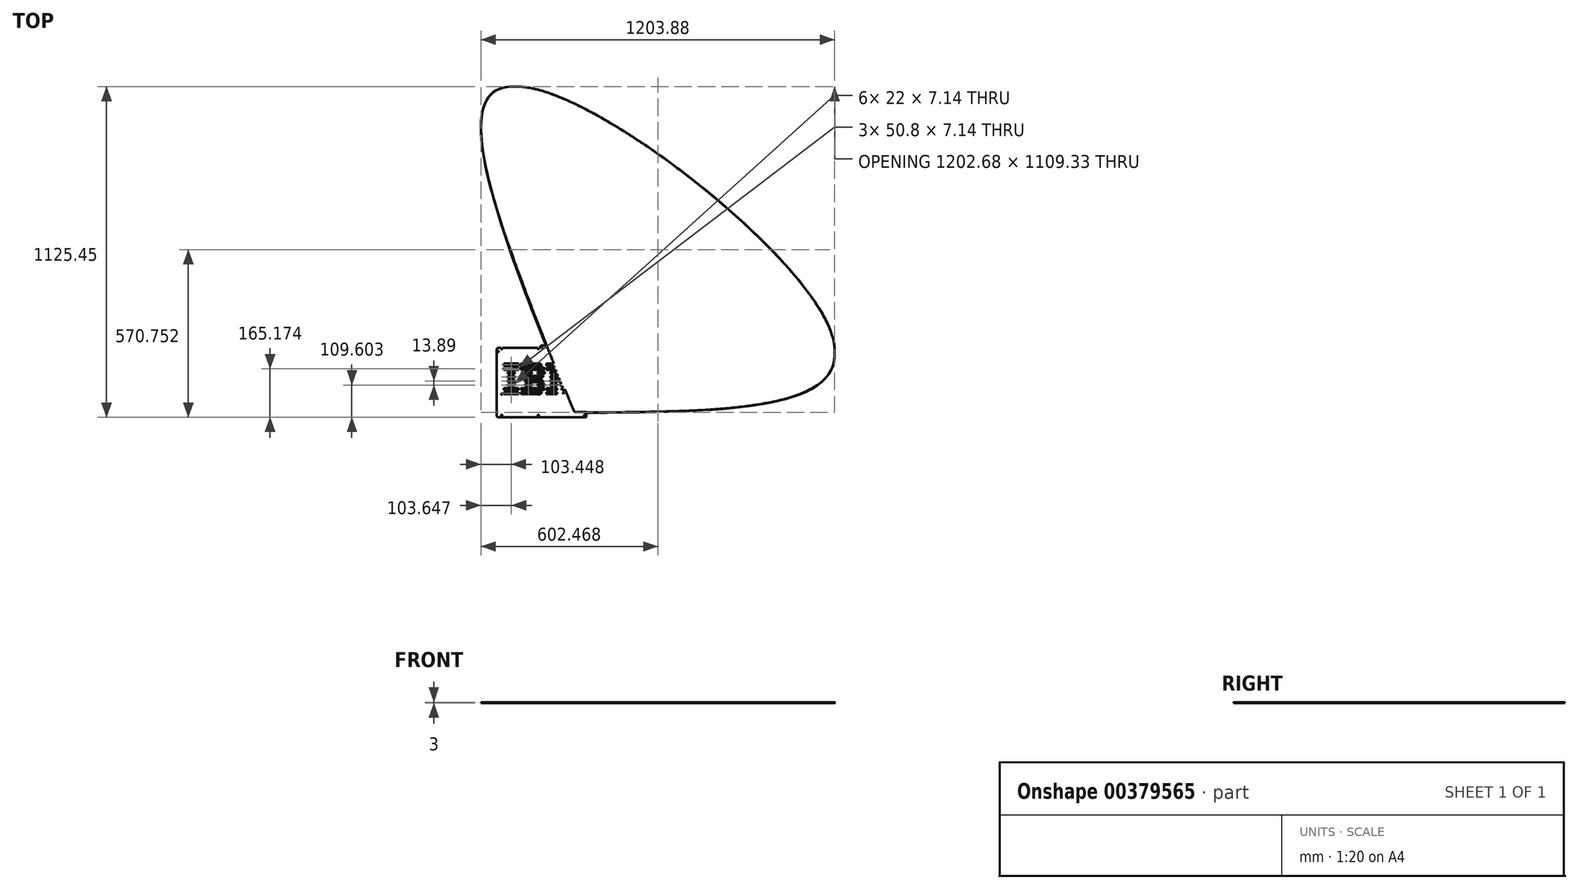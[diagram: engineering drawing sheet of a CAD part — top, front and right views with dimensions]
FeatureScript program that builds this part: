
annotation { "Feature Type Name" : "Feature", "Feature Type Description" : "" }
export const myFeature = defineFeature(function(context is Context, id is Id, definition is map)
    precondition{}
    {
        {
            var Q0;
            Q0=qCreatedBy(makeId("Top.planeOp"),FACE);
            var sketch = newSketch(context, id + "F0", { "sketchPlane" : qUnion([Q0])});
            skLineSegment(sketch, "E0.bottom", {"start": v(-143.4, -124.67) * mm, "end": v(153.48, -124.67) * mm});
            skLineSegment(sketch, "E0.left", {"start": v(-147.36, -120.71) * mm, "end": v(-147.36, 107.08) * mm});
            skLineSegment(sketch, "E0.right", {"start": v(157.44, -120.71) * mm, "end": v(157.44, 115.08) * mm});
            skArc(sketch, "E1", {"start": v(-132.83, 108.88) * mm, "mid": v(-130.85, 106.9) * mm, "end": v(-128.87, 108.88) * mm});
            skCircle(sketch, "E2", {"center": v(-130.85, -118.45) * mm, "radius": 1.98 * mm});
            skCircle(sketch, "E3", {"center": v(-130.85, -46.06) * mm, "radius": 1.98 * mm});
            skCircle(sketch, "E4", {"center": v(-6.4, -118.45) * mm, "radius": 1.98 * mm});
            skArc(sketch, "E5", {"start": v(-8.37, 108.88) * mm, "mid": v(-6.4, 106.9) * mm, "end": v(-4.4, 108.88) * mm});
            skCircle(sketch, "E6", {"center": v(151.09, 86.02) * mm, "radius": 1.98 * mm});
            skCircle(sketch, "E7", {"center": v(151.09, -118.32) * mm, "radius": 1.98 * mm});
            skCircle(sketch, "E8", {"center": v(151.09, -45.93) * mm, "radius": 1.98 * mm});
            skPoint(sketch, "E9.visualSharp", {"position": v(-147.36, -124.67) * mm});
            skArc(sketch, "E9.filletArc", {"start": v(-147.36, -120.71) * mm, "mid": v(-146.2, -123.51) * mm, "end": v(-143.4, -124.67) * mm});
            skPoint(sketch, "E10.visualSharp", {"position": v(157.44, 119.04) * mm});
            skArc(sketch, "E10.filletArc", {"start": v(157.44, 115.08) * mm, "mid": v(156.28, 117.88) * mm, "end": v(153.48, 119.04) * mm});
            skPoint(sketch, "E11.visualSharp", {"position": v(157.44, -124.67) * mm});
            skArc(sketch, "E11.filletArc", {"start": v(153.48, -124.67) * mm, "mid": v(156.28, -123.51) * mm, "end": v(157.44, -120.71) * mm});
            skLineSegment(sketch, "E12", {"start": v(88.4, 36.93) * mm, "end": v(136.8, 36.93) * mm});
            skLineSegment(sketch, "E13", {"start": v(136.8, 44.06) * mm, "end": v(90.8, 44.06) * mm});
            skLineSegment(sketch, "E14", {"start": v(-109.18, 23.03) * mm, "end": v(-87.18, 23.03) * mm});
            skFitSpline(sketch, "E15", {"points": [v(15, 36.93) * mm, v(14.06, 42.43) * mm, v(12.42, 44.06) * mm]});
            skLineSegment(sketch, "E16", {"start": v(67, 44.06) * mm, "end": v(20.8, 44.06) * mm});
            skLineSegment(sketch, "E17", {"start": v(-87.18, 30.18) * mm, "end": v(-109.18, 30.18) * mm});
            skLineSegment(sketch, "E18", {"start": v(-51.19, 23.03) * mm, "end": v(-29.19, 23.03) * mm});
            skLineSegment(sketch, "E19", {"start": v(-7.79, 23.03) * mm, "end": v(14.21, 23.03) * mm});
            skLineSegment(sketch, "E20", {"start": v(35.4, 30.18) * mm, "end": v(35.4, 23.03) * mm});
            skLineSegment(sketch, "E21", {"start": v(-29.19, 30.18) * mm, "end": v(-51.19, 30.18) * mm});
            skLineSegment(sketch, "E22", {"start": v(71.81, 30.18) * mm, "end": v(35.4, 30.18) * mm});
            skLineSegment(sketch, "E23", {"start": v(86.01, 30.18) * mm, "end": v(83.4, 23.03) * mm});
            skLineSegment(sketch, "E24", {"start": v(-65.78, 44.06) * mm, "end": v(-65.78, 36.93) * mm});
            skLineSegment(sketch, "E25", {"start": v(-109.18, 30.18) * mm, "end": v(-109.18, 23.03) * mm});
            skLineSegment(sketch, "E26", {"start": v(136.8, 36.93) * mm, "end": v(136.8, 44.06) * mm});
            skLineSegment(sketch, "E27", {"start": v(-7.79, 30.18) * mm, "end": v(-7.79, 23.03) * mm});
            skLineSegment(sketch, "E28", {"start": v(35.4, 23.03) * mm, "end": v(74.41, 23.03) * mm});
            skLineSegment(sketch, "E29", {"start": v(83.4, 23.03) * mm, "end": v(122.6, 23.03) * mm});
            skLineSegment(sketch, "E30", {"start": v(122.6, 23.03) * mm, "end": v(122.6, 30.18) * mm});
            skLineSegment(sketch, "E31", {"start": v(-10.58, 57.97) * mm, "end": v(-65.78, 57.97) * mm});
            skLineSegment(sketch, "E32", {"start": v(-109.18, 16.28) * mm, "end": v(-109.18, 9.14) * mm});
            skLineSegment(sketch, "E33", {"start": v(122.6, 30.18) * mm, "end": v(86.01, 30.18) * mm});
            skLineSegment(sketch, "E34", {"start": v(-123.78, 57.97) * mm, "end": v(-123.78, 50.82) * mm});
            skLineSegment(sketch, "E35", {"start": v(74.41, 23.03) * mm, "end": v(71.81, 30.18) * mm});
            skLineSegment(sketch, "E36", {"start": v(-109.18, 9.14) * mm, "end": v(-87.18, 9.14) * mm});
            skLineSegment(sketch, "E37", {"start": v(20.8, 36.93) * mm, "end": v(69.4, 36.93) * mm});
            skLineSegment(sketch, "E38", {"start": v(-87.18, 9.14) * mm, "end": v(-87.18, 16.28) * mm});
            skLineSegment(sketch, "E39", {"start": v(-87.18, 16.28) * mm, "end": v(-109.18, 16.28) * mm});
            skLineSegment(sketch, "E40", {"start": v(-123.78, 36.93) * mm, "end": v(-72.98, 36.93) * mm});
            skLineSegment(sketch, "E41", {"start": v(-51.19, 16.28) * mm, "end": v(-51.19, 9.14) * mm});
            skLineSegment(sketch, "E42", {"start": v(12.42, 44.06) * mm, "end": v(-65.78, 44.06) * mm});
            skLineSegment(sketch, "E43", {"start": v(93.4, 50.82) * mm, "end": v(136.8, 50.82) * mm});
            skLineSegment(sketch, "E44", {"start": v(-51.19, 9.14) * mm, "end": v(5, 9.14) * mm});
            skLineSegment(sketch, "E45", {"start": v(64.6, 50.82) * mm, "end": v(62, 57.97) * mm});
            skLineSegment(sketch, "E46", {"start": v(-87.18, 23.03) * mm, "end": v(-87.18, 30.18) * mm});
            skLineSegment(sketch, "E47", {"start": v(15.61, 30.18) * mm, "end": v(-7.79, 30.18) * mm});
            skLineSegment(sketch, "E48", {"start": v(136.8, 57.97) * mm, "end": v(96, 57.97) * mm});
            skLineSegment(sketch, "E49", {"start": v(136.8, 50.82) * mm, "end": v(136.8, 57.97) * mm});
            skLineSegment(sketch, "E50", {"start": v(-123.78, 44.08) * mm, "end": v(-123.78, 36.93) * mm});
            skLineSegment(sketch, "E51", {"start": v(-72.98, 50.82) * mm, "end": v(-72.98, 57.97) * mm});
            skLineSegment(sketch, "E52", {"start": v(-72.98, 44.08) * mm, "end": v(-123.78, 44.08) * mm});
            skLineSegment(sketch, "E53", {"start": v(-29.19, 23.03) * mm, "end": v(-29.19, 30.18) * mm});
            skLineSegment(sketch, "E54", {"start": v(96, 57.97) * mm, "end": v(93.4, 50.82) * mm});
            skFitSpline(sketch, "E55", {"points": [v(14.21, 23.03) * mm, v(15.61, 26.8) * mm, v(15.61, 30.18) * mm]});
            skLineSegment(sketch, "E56", {"start": v(-51.19, 30.18) * mm, "end": v(-51.19, 23.03) * mm});
            skLineSegment(sketch, "E57", {"start": v(-72.98, 57.97) * mm, "end": v(-123.78, 57.97) * mm});
            skLineSegment(sketch, "E58", {"start": v(62, 57.97) * mm, "end": v(20.8, 57.97) * mm});
            skLineSegment(sketch, "E59", {"start": v(-72.98, 36.93) * mm, "end": v(-72.98, 44.08) * mm});
            skLineSegment(sketch, "E60", {"start": v(-123.78, 50.82) * mm, "end": v(-72.98, 50.82) * mm});
            skFitSpline(sketch, "E61", {"points": [v(6.6, 50.82) * mm, v(-0.79, 57.97) * mm, v(-10.58, 57.97) * mm]});
            skLineSegment(sketch, "E62", {"start": v(-65.78, 57.97) * mm, "end": v(-65.78, 50.82) * mm});
            skLineSegment(sketch, "E63", {"start": v(-65.78, 50.82) * mm, "end": v(6.6, 50.82) * mm});
            skLineSegment(sketch, "E64", {"start": v(20.8, 50.82) * mm, "end": v(64.6, 50.82) * mm});
            skLineSegment(sketch, "E65", {"start": v(20.8, 57.97) * mm, "end": v(20.8, 50.82) * mm});
            skLineSegment(sketch, "E66", {"start": v(-65.78, 36.93) * mm, "end": v(15, 36.93) * mm});
            skLineSegment(sketch, "E67", {"start": v(20.8, 44.06) * mm, "end": v(20.8, 36.93) * mm});
            skLineSegment(sketch, "E68", {"start": v(69.4, 36.93) * mm, "end": v(67, 44.06) * mm});
            skLineSegment(sketch, "E69", {"start": v(90.8, 44.06) * mm, "end": v(88.4, 36.93) * mm});
            skFitSpline(sketch, "E70", {"points": [v(5, 9.14) * mm, v(9.7, 12.8) * mm, v(11.2, 16.28) * mm]});
            skLineSegment(sketch, "E71", {"start": v(-87.18, -18.64) * mm, "end": v(-87.18, -11.5) * mm});
            skLineSegment(sketch, "E72", {"start": v(57.4, -18.64) * mm, "end": v(57.4, -11.5) * mm});
            skLineSegment(sketch, "E73", {"start": v(-51.19, -18.64) * mm, "end": v(-29.19, -18.64) * mm});
            skLineSegment(sketch, "E74", {"start": v(-29.19, -11.5) * mm, "end": v(-51.19, -11.5) * mm});
            skLineSegment(sketch, "E75", {"start": v(58.8, 9.14) * mm, "end": v(99.1, 9.14) * mm});
            skLineSegment(sketch, "E76", {"start": v(79.11, 10.23) * mm, "end": v(76.91, 16.28) * mm});
            skLineSegment(sketch, "E77", {"start": v(76.91, 16.28) * mm, "end": v(35.4, 16.28) * mm});
            skLineSegment(sketch, "E78", {"start": v(57.4, -4.75) * mm, "end": v(57.4, 2.4) * mm});
            skLineSegment(sketch, "E79", {"start": v(35.4, 16.28) * mm, "end": v(35.4, 9.14) * mm});
            skLineSegment(sketch, "E80", {"start": v(14.21, -11.5) * mm, "end": v(-7.79, -11.5) * mm});
            skLineSegment(sketch, "E81", {"start": v(122.6, 16.28) * mm, "end": v(81.3, 16.28) * mm});
            skLineSegment(sketch, "E82", {"start": v(66.4, -11.5) * mm, "end": v(68.98, -18.64) * mm});
            skLineSegment(sketch, "E83", {"start": v(122.6, 2.4) * mm, "end": v(100.6, 2.4) * mm});
            skLineSegment(sketch, "E84", {"start": v(89.24, -18.64) * mm, "end": v(91.84, -11.5) * mm});
            skLineSegment(sketch, "E85", {"start": v(91.84, -11.5) * mm, "end": v(66.4, -11.5) * mm});
            skLineSegment(sketch, "E86", {"start": v(11.2, 16.28) * mm, "end": v(-51.19, 16.28) * mm});
            skLineSegment(sketch, "E87", {"start": v(100.6, -11.5) * mm, "end": v(100.6, -18.64) * mm});
            skLineSegment(sketch, "E88", {"start": v(100.6, -18.64) * mm, "end": v(122.6, -18.64) * mm});
            skFitSpline(sketch, "E89", {"points": [v(15.61, -18.64) * mm, v(15.61, -15.27) * mm, v(14.21, -11.5) * mm]});
            skLineSegment(sketch, "E90", {"start": v(122.6, -11.5) * mm, "end": v(100.6, -11.5) * mm});
            skLineSegment(sketch, "E91", {"start": v(-123.38, -32.54) * mm, "end": v(-72.58, -32.54) * mm});
            skLineSegment(sketch, "E92", {"start": v(122.6, -18.64) * mm, "end": v(122.6, -11.5) * mm});
            skLineSegment(sketch, "E93", {"start": v(-109.18, -4.75) * mm, "end": v(-87.18, -4.75) * mm});
            skLineSegment(sketch, "E94", {"start": v(-72.58, -32.54) * mm, "end": v(-72.58, -25.39) * mm});
            skLineSegment(sketch, "E95", {"start": v(64.07, -4.75) * mm, "end": v(94.28, -4.75) * mm});
            skLineSegment(sketch, "E96", {"start": v(-109.18, 2.4) * mm, "end": v(-109.18, -4.75) * mm});
            skLineSegment(sketch, "E97", {"start": v(100.6, 2.4) * mm, "end": v(100.6, -4.75) * mm});
            skLineSegment(sketch, "E98", {"start": v(57.4, 13.12) * mm, "end": v(58.8, 9.14) * mm});
            skLineSegment(sketch, "E99", {"start": v(94.28, -4.75) * mm, "end": v(96.81, 2.4) * mm});
            skLineSegment(sketch, "E100", {"start": v(57.4, -11.5) * mm, "end": v(35.4, -11.5) * mm});
            skLineSegment(sketch, "E101", {"start": v(100.6, 13.12) * mm, "end": v(100.6, 9.14) * mm});
            skLineSegment(sketch, "E102", {"start": v(5, 2.4) * mm, "end": v(-51.19, 2.4) * mm});
            skLineSegment(sketch, "E103", {"start": v(68.98, -18.64) * mm, "end": v(89.24, -18.64) * mm});
            skLineSegment(sketch, "E104", {"start": v(-123.38, -25.39) * mm, "end": v(-123.38, -32.54) * mm});
            skLineSegment(sketch, "E105", {"start": v(100.6, 9.14) * mm, "end": v(122.6, 9.14) * mm});
            skLineSegment(sketch, "E106", {"start": v(-65.78, -25.39) * mm, "end": v(-65.78, -32.54) * mm});
            skLineSegment(sketch, "E107", {"start": v(-72.58, -25.39) * mm, "end": v(-123.38, -25.39) * mm});
            skLineSegment(sketch, "E108", {"start": v(35.4, -18.64) * mm, "end": v(57.4, -18.64) * mm});
            skLineSegment(sketch, "E109", {"start": v(122.6, 9.14) * mm, "end": v(122.6, 16.28) * mm});
            skLineSegment(sketch, "E110", {"start": v(35.4, 2.4) * mm, "end": v(35.4, -4.75) * mm});
            skLineSegment(sketch, "E111", {"start": v(-109.18, -18.64) * mm, "end": v(-87.18, -18.64) * mm});
            skLineSegment(sketch, "E112", {"start": v(99.1, 9.14) * mm, "end": v(100.6, 13.12) * mm});
            skLineSegment(sketch, "E113", {"start": v(35.4, 9.14) * mm, "end": v(57.4, 9.14) * mm});
            skLineSegment(sketch, "E114", {"start": v(81.3, 16.28) * mm, "end": v(79.11, 10.23) * mm});
            skLineSegment(sketch, "E115", {"start": v(-87.18, 2.4) * mm, "end": v(-109.18, 2.4) * mm});
            skLineSegment(sketch, "E116", {"start": v(57.4, 2.4) * mm, "end": v(35.4, 2.4) * mm});
            skLineSegment(sketch, "E117", {"start": v(100.6, -4.75) * mm, "end": v(122.6, -4.75) * mm});
            skFitSpline(sketch, "E118", {"points": [v(11.2, -4.75) * mm, v(9.7, -1.28) * mm, v(5, 2.4) * mm]});
            skLineSegment(sketch, "E119", {"start": v(61.4, 2.4) * mm, "end": v(64.07, -4.75) * mm});
            skLineSegment(sketch, "E120", {"start": v(-51.19, 2.4) * mm, "end": v(-51.19, -4.75) * mm});
            skLineSegment(sketch, "E121", {"start": v(96.81, 2.4) * mm, "end": v(61.4, 2.4) * mm});
            skLineSegment(sketch, "E122", {"start": v(57.4, 9.14) * mm, "end": v(57.4, 13.12) * mm});
            skLineSegment(sketch, "E123", {"start": v(-87.18, -4.75) * mm, "end": v(-87.18, 2.4) * mm});
            skLineSegment(sketch, "E124", {"start": v(35.4, -4.75) * mm, "end": v(57.4, -4.75) * mm});
            skLineSegment(sketch, "E125", {"start": v(-51.19, -4.75) * mm, "end": v(11.2, -4.75) * mm});
            skLineSegment(sketch, "E126", {"start": v(-109.18, -11.5) * mm, "end": v(-109.18, -18.64) * mm});
            skLineSegment(sketch, "E127", {"start": v(-51.19, -11.5) * mm, "end": v(-51.19, -18.64) * mm});
            skLineSegment(sketch, "E128", {"start": v(-87.18, -11.5) * mm, "end": v(-109.18, -11.5) * mm});
            skLineSegment(sketch, "E129", {"start": v(-29.19, -18.64) * mm, "end": v(-29.19, -11.5) * mm});
            skLineSegment(sketch, "E130", {"start": v(-7.79, -11.5) * mm, "end": v(-7.79, -18.64) * mm});
            skLineSegment(sketch, "E131", {"start": v(-7.79, -18.64) * mm, "end": v(15.61, -18.64) * mm});
            skLineSegment(sketch, "E132", {"start": v(35.4, -11.5) * mm, "end": v(35.4, -18.64) * mm});
            skLineSegment(sketch, "E133", {"start": v(122.6, -4.75) * mm, "end": v(122.6, 2.4) * mm});
            skLineSegment(sketch, "E134", {"start": v(137.2, -25.39) * mm, "end": v(100.6, -25.39) * mm});
            skLineSegment(sketch, "E135", {"start": v(137.2, -39.29) * mm, "end": v(100.6, -39.29) * mm});
            skLineSegment(sketch, "E136", {"start": v(57.4, -32.54) * mm, "end": v(57.4, -25.39) * mm});
            skLineSegment(sketch, "E137", {"start": v(76.43, -39.29) * mm, "end": v(78.98, -46.4) * mm});
            skFitSpline(sketch, "E138", {"points": [v(-10.58, -46.42) * mm, v(-0.79, -46.42) * mm, v(6.6, -39.29) * mm]});
            skLineSegment(sketch, "E139", {"start": v(57.4, -46.43) * mm, "end": v(57.4, -39.29) * mm});
            skLineSegment(sketch, "E140", {"start": v(78.98, -46.4) * mm, "end": v(79.42, -46.42) * mm});
            skLineSegment(sketch, "E141", {"start": v(100.6, -46.43) * mm, "end": v(137.2, -46.43) * mm});
            skLineSegment(sketch, "E142", {"start": v(15, -25.39) * mm, "end": v(-65.78, -25.39) * mm});
            skLineSegment(sketch, "E143", {"start": v(21.2, -32.54) * mm, "end": v(57.4, -32.54) * mm});
            skLineSegment(sketch, "E144", {"start": v(6.6, -39.29) * mm, "end": v(-65.78, -39.29) * mm});
            skLineSegment(sketch, "E145", {"start": v(-72.58, -39.29) * mm, "end": v(-123.38, -39.29) * mm});
            skLineSegment(sketch, "E146", {"start": v(-123.38, -46.43) * mm, "end": v(-72.58, -46.43) * mm});
            skLineSegment(sketch, "E147", {"start": v(84.36, -32.54) * mm, "end": v(86.85, -25.39) * mm});
            skFitSpline(sketch, "E148", {"points": [v(12.42, -32.54) * mm, v(14.06, -30.9) * mm, v(15, -25.39) * mm]});
            skLineSegment(sketch, "E149", {"start": v(100.6, -25.39) * mm, "end": v(100.6, -32.54) * mm});
            skLineSegment(sketch, "E150", {"start": v(137.2, -32.54) * mm, "end": v(137.2, -25.39) * mm});
            skLineSegment(sketch, "E151", {"start": v(100.6, -32.54) * mm, "end": v(137.2, -32.54) * mm});
            skLineSegment(sketch, "E152", {"start": v(-123.38, -39.29) * mm, "end": v(-123.38, -46.43) * mm});
            skLineSegment(sketch, "E153", {"start": v(-65.78, -39.29) * mm, "end": v(-65.78, -46.42) * mm});
            skLineSegment(sketch, "E154", {"start": v(21.2, -46.43) * mm, "end": v(57.4, -46.43) * mm});
            skLineSegment(sketch, "E155", {"start": v(57.4, -39.29) * mm, "end": v(21.2, -39.29) * mm});
            skLineSegment(sketch, "E156", {"start": v(74.06, -32.54) * mm, "end": v(84.36, -32.54) * mm});
            skLineSegment(sketch, "E157", {"start": v(100.6, -39.29) * mm, "end": v(100.6, -46.43) * mm});
            skLineSegment(sketch, "E158", {"start": v(79.42, -46.42) * mm, "end": v(82, -39.29) * mm});
            skLineSegment(sketch, "E159", {"start": v(86.85, -25.39) * mm, "end": v(71.4, -25.39) * mm});
            skLineSegment(sketch, "E160", {"start": v(137.2, -46.43) * mm, "end": v(137.2, -39.29) * mm});
            skLineSegment(sketch, "E161", {"start": v(71.4, -25.39) * mm, "end": v(74.06, -32.54) * mm});
            skLineSegment(sketch, "E162", {"start": v(-65.78, -46.42) * mm, "end": v(-10.58, -46.42) * mm});
            skLineSegment(sketch, "E163", {"start": v(57.4, -25.39) * mm, "end": v(21.2, -25.39) * mm});
            skLineSegment(sketch, "E164", {"start": v(21.2, -39.29) * mm, "end": v(21.2, -46.43) * mm});
            skLineSegment(sketch, "E165", {"start": v(-65.78, -32.54) * mm, "end": v(12.42, -32.54) * mm});
            skLineSegment(sketch, "E166", {"start": v(21.2, -25.39) * mm, "end": v(21.2, -32.54) * mm});
            skLineSegment(sketch, "E167", {"start": v(-72.58, -46.43) * mm, "end": v(-72.58, -39.29) * mm});
            skLineSegment(sketch, "E168", {"start": v(82, -39.29) * mm, "end": v(76.43, -39.29) * mm});
            skFitSpline(sketch, "E169", {"points": [v(124, -93.23) * mm, v(1000, 123.55) * mm, v(-92.62, 1000) * mm, v(122.64, -91.7) * mm]});
            skFitSpline(sketch, "E170", {"points": [v(119.47, -90.26) * mm, v(1000, 118.7) * mm, v(-90.07, 1000) * mm, v(117.3, -90.03) * mm]});
            skFitSpline(sketch, "E171", {"points": [v(122.22, -91.42) * mm, v(1000, 121.38) * mm, v(-90.88, 1000) * mm, v(120.51, -90.51) * mm]});
            skLineSegment(sketch, "E172", {"start": v(112.38, -108.72) * mm, "end": v(113.87, -106.96) * mm});
            skFitSpline(sketch, "E173", {"points": [v(111.69, -105.36) * mm, v(1000, 111.26) * mm, v(-106.35, 1000) * mm, v(110.86, -107.27) * mm]});
            skFitSpline(sketch, "E174", {"points": [v(113.87, -106.96) * mm, v(1000, 114.95) * mm, v(-105.67, 1000) * mm, v(115.38, -105.2) * mm]});
            skFitSpline(sketch, "E175", {"points": [v(116.46, -90.15) * mm, v(1000, 114.61) * mm, v(-90.45, 1000) * mm, v(112.75, -91.55) * mm]});
            skFitSpline(sketch, "E176", {"points": [v(116.66, -105.53) * mm, v(1000, 116.71) * mm, v(-105.53, 1000) * mm, v(116.77, -105.58) * mm]});
            skFitSpline(sketch, "E177", {"points": [v(117.15, -107.32) * mm, v(1000, 117.34) * mm, v(-108.17, 1000) * mm, v(117.52, -109) * mm]});
            skLineSegment(sketch, "E178", {"start": v(117.56, -109.17) * mm, "end": v(117.63, -109.48) * mm});
            skLineSegment(sketch, "E179", {"start": v(117.63, -109.48) * mm, "end": v(118.1, -109.46) * mm});
            skFitSpline(sketch, "E180", {"points": [v(111.29, -108.05) * mm, v(1000, 111.61) * mm, v(-108.27, 1000) * mm, v(112, -108.5) * mm]});
            skFitSpline(sketch, "E181", {"points": [v(118.1, -109.46) * mm, v(1000, 118.35) * mm, v(-109.46, 1000) * mm, v(118.8, -109.44) * mm]});
            skFitSpline(sketch, "E182", {"points": [v(111.69, -93) * mm, v(1000, 109.34) * mm, v(-96.17, 1000) * mm, v(109.6, -100.36) * mm]});
            skFitSpline(sketch, "E183", {"points": [v(112.5, -103.51) * mm, v(1000, 112.48) * mm, v(-103.54, 1000) * mm, v(112.12, -104.37) * mm]});
            skLineSegment(sketch, "E184", {"start": v(110.8, -107.41) * mm, "end": v(110.7, -107.66) * mm});
            skLineSegment(sketch, "E185", {"start": v(110.7, -107.66) * mm, "end": v(111.29, -108.05) * mm});
            skFitSpline(sketch, "E186", {"points": [v(115.44, -105.23) * mm, v(1000, 115.6) * mm, v(-105.29, 1000) * mm, v(116.56, -105.53) * mm]});
            skFitSpline(sketch, "E187", {"points": [v(116.78, -105.65) * mm, v(1000, 116.8) * mm, v(-105.72, 1000) * mm, v(116.97, -106.47) * mm]});
            skFitSpline(sketch, "E188", {"points": [v(112.33, -103.26) * mm, v(1000, 112.43) * mm, v(-103.37, 1000) * mm, v(112.5, -103.48) * mm]});
            skLineSegment(sketch, "E189", {"start": v(112.13, -108.58) * mm, "end": v(112.38, -108.72) * mm});
            skFitSpline(sketch, "E190", {"points": [v(119.66, -108.76) * mm, v(1000, 119.71) * mm, v(-108.06, 1000) * mm, v(119.93, -105.39) * mm]});
            skFitSpline(sketch, "E191", {"points": [v(119.08, -109.42) * mm, v(1000, 119.66) * mm, v(-109.38, 1000) * mm, v(119.61, -109.43) * mm]});
            skFitSpline(sketch, "E192", {"points": [v(121.3, -104.86) * mm, v(1000, 121.33) * mm, v(-104.86, 1000) * mm, v(121.89, -105.34) * mm]});
            skFitSpline(sketch, "E193", {"points": [v(119.94, -105.38) * mm, v(120.24, -105.27) * mm, v(120.59, -105.12) * mm]});
            skFitSpline(sketch, "E194", {"points": [v(120.59, -105.12) * mm, v(1000, 120.95) * mm, v(-104.98, 1000) * mm, v(121.26, -104.86) * mm]});
            skFitSpline(sketch, "E195", {"points": [v(122.53, -105.93) * mm, v(1000, 123.17) * mm, v(-106.5, 1000) * mm, v(123.91, -107.18) * mm]});
            skFitSpline(sketch, "E196", {"points": [v(124.17, -107.42) * mm, v(1000, 124.44) * mm, v(-107.65, 1000) * mm, v(124.68, -107.85) * mm]});
            skFitSpline(sketch, "E197", {"points": [v(124.73, -107.85) * mm, v(1000, 124.79) * mm, v(-107.85, 1000) * mm, v(125.7, -107.13) * mm]});
            skLineSegment(sketch, "E198", {"start": v(126.23, -106.64) * mm, "end": v(126.04, -106.32) * mm});
            skFitSpline(sketch, "E199", {"points": [v(126.04, -106.32) * mm, v(1000, 125.94) * mm, v(-106.14, 1000) * mm, v(125.43, -105.28) * mm]});
            skFitSpline(sketch, "E200", {"points": [v(124.9, -104.4) * mm, v(1000, 124.38) * mm, v(-103.53, 1000) * mm, v(123.95, -102.8) * mm]});
            skLineSegment(sketch, "E201", {"start": v(126.07, -106.8) * mm, "end": v(126.23, -106.64) * mm});
            skFitSpline(sketch, "E202", {"points": [v(123.95, -102.79) * mm, v(1000, 123.95) * mm, v(-102.77, 1000) * mm, v(124.08, -102.55) * mm]});
            skLineSegment(sketch, "E203", {"start": v(125.54, -98.4) * mm, "end": v(123.87, -98.41) * mm});
            skLineSegment(sketch, "E204", {"start": v(125.5, -98.72) * mm, "end": v(125.54, -98.4) * mm});
            skLineSegment(sketch, "E205", {"start": v(122.2, -98.43) * mm, "end": v(122.17, -98.78) * mm});
            skLineSegment(sketch, "E206", {"start": v(123.87, -98.41) * mm, "end": v(122.2, -98.43) * mm});
            skFitSpline(sketch, "E207", {"points": [v(122.17, -98.78) * mm, v(1000, 122.1) * mm, v(-99.41, 1000) * mm, v(121.78, -100.18) * mm]});
            skFitSpline(sketch, "E208", {"points": [v(121.35, -100.71) * mm, v(1000, 121.07) * mm, v(-101.08, 1000) * mm, v(120.34, -101.66) * mm]});
            skFitSpline(sketch, "E209", {"points": [v(124.24, -102.3) * mm, v(1000, 124.95) * mm, v(-101.24, 1000) * mm, v(125.4, -99.98) * mm]});
            skFitSpline(sketch, "E210", {"points": [v(115.14, -101.31) * mm, v(1000, 114.83) * mm, v(-101, 1000) * mm, v(114.78, -100.92) * mm]});
            skFitSpline(sketch, "E211", {"points": [v(117.37, -102.44) * mm, v(1000, 116.45) * mm, v(-102.32, 1000) * mm, v(115.85, -102.02) * mm]});
            skFitSpline(sketch, "E212", {"points": [v(116.5, -99.88) * mm, v(1000, 121.2) * mm, v(-97.14, 1000) * mm, v(124.97, -94.92) * mm]});
            skFitSpline(sketch, "E213", {"points": [v(114.84, -100.86) * mm, v(1000, 114.88) * mm, v(-100.82, 1000) * mm, v(115.62, -100.38) * mm]});
            skFitSpline(sketch, "E214", {"points": [v(124.98, -94.87) * mm, v(1000, 125.01) * mm, v(-94.79, 1000) * mm, v(124.4, -93.76) * mm]});
            skFitSpline(sketch, "E215", {"points": [v(119.87, -101.9) * mm, v(1000, 119) * mm, v(-102.35, 1000) * mm, v(118.14, -102.53) * mm]});
            skLineSegment(sketch, "E216", {"start": v(-142.36, 122.65) * mm, "end": v(-142.36, 88.24) * mm, "construction": true});
            skLineSegment(sketch, "E217", {"start": v(-152.8, 99.04) * mm, "end": v(-133.28, 99.04) * mm, "construction": true});
            skCircle(sketch, "E218", {"center": v(-142.36, 99.04) * mm, "radius": 1.5 * mm});
            skLineSegment(sketch, "E219", {"start": v(-149.74, 111.04) * mm, "end": v(-132.83, 111.04) * mm, "construction": true});
            skLineSegment(sketch, "E220", {"start": v(0.6, 122.7) * mm, "end": v(0.6, 103.54) * mm, "construction": true});
            skLineSegment(sketch, "E221", {"start": v(8.6, 127.36) * mm, "end": v(8.6, 95.97) * mm, "construction": true});
            skLineSegment(sketch, "E222", {"start": v(-151.16, 108.88) * mm, "end": v(25.53, 108.88) * mm, "construction": true});
            skCircle(sketch, "E223", {"center": v(8.6, 108.88) * mm, "radius": 1.5 * mm});
            skLineSegment(sketch, "E224", {"start": v(0.6, 115.08) * mm, "end": v(0.6, 111.04) * mm});
            skLineSegment(sketch, "E225", {"start": v(0.6, 111.04) * mm, "end": v(-4.4, 111.04) * mm});
            skLineSegment(sketch, "E226.trimOffspring", {"start": v(4.57, 119.04) * mm, "end": v(153.48, 119.04) * mm});
            skPoint(sketch, "E227.visualSharp", {"position": v(-147.36, 111.04) * mm});
            skArc(sketch, "E227.filletArc", {"start": v(-143.4, 111.04) * mm, "mid": v(-146.2, 109.88) * mm, "end": v(-147.36, 107.08) * mm});
            skPoint(sketch, "E228.visualSharp", {"position": v(0.6, 119.04) * mm});
            skArc(sketch, "E228.filletArc", {"start": v(4.57, 119.04) * mm, "mid": v(1.77, 117.88) * mm, "end": v(0.6, 115.08) * mm});
            skLineSegment(sketch, "E229", {"start": v(-132.83, 108.88) * mm, "end": v(-132.83, 111.04) * mm});
            skLineSegment(sketch, "E230", {"start": v(-128.87, 108.88) * mm, "end": v(-128.87, 111.04) * mm});
            skLineSegment(sketch, "E231.trimOffspring", {"start": v(-132.83, 111.04) * mm, "end": v(-143.4, 111.04) * mm});
            skLineSegment(sketch, "E232", {"start": v(-8.37, 108.88) * mm, "end": v(-8.37, 111.04) * mm});
            skLineSegment(sketch, "E233", {"start": v(-4.4, 108.88) * mm, "end": v(-4.4, 111.04) * mm});
            skLineSegment(sketch, "E234.trimOffspring", {"start": v(-4.4, 111.04) * mm, "end": v(17.39, 111.04) * mm, "construction": true});
            skLineSegment(sketch, "E235.trimOffspring", {"start": v(-8.37, 111.04) * mm, "end": v(-128.87, 111.04) * mm});
            skSolve(sketch);
        }
        {
            var Q0;
            Q0 = qSketchRegion(id + "F0", true);
            extrude(context, id + "F1", {"entities" : qUnion([Q0]), "depth" : 3 * mm});
        }
    });
